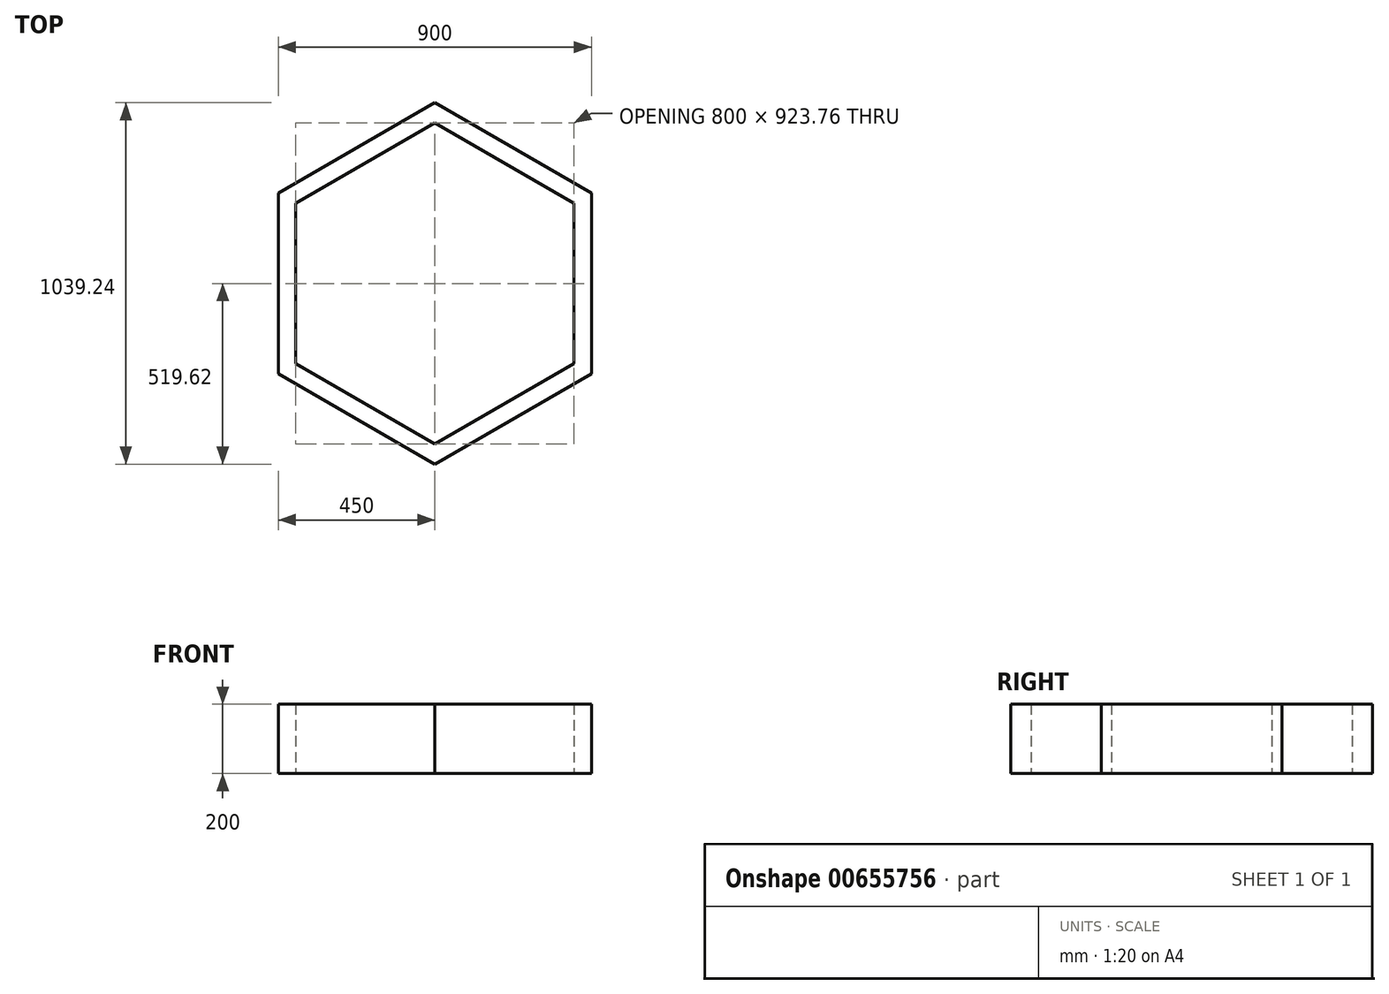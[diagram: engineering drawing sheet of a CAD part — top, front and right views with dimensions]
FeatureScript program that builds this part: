
annotation { "Feature Type Name" : "Feature", "Feature Type Description" : "" }
export const myFeature = defineFeature(function(context is Context, id is Id, definition is map)
    precondition{}
    {
        {
            var Q0;
            Q0=qCreatedBy(makeId("Top.planeOp"),FACE);
            var sketch = newSketch(context, id + "F0", { "sketchPlane" : qUnion([Q0])});
            skCircle(sketch, "E0.cCircle", {"center": v(0, 0) * mm, "radius": 450 * mm, "construction": true});
            skLineSegment(sketch, "E0.0", {"start": v(450, 259.8) * mm, "end": v(450, -259.8) * mm});
            skLineSegment(sketch, "E0.1", {"start": v(450, -259.8) * mm, "end": v(0, -519.62) * mm});
            skLineSegment(sketch, "E0.2", {"start": v(0, -519.62) * mm, "end": v(-450, -259.8) * mm});
            skLineSegment(sketch, "E0.3", {"start": v(-450, -259.8) * mm, "end": v(-450, 259.8) * mm});
            skLineSegment(sketch, "E0.4", {"start": v(-450, 259.8) * mm, "end": v(0, 519.62) * mm});
            skLineSegment(sketch, "E0.5", {"start": v(0, 519.62) * mm, "end": v(450, 259.8) * mm});
            skPoint(sketch, "E0.0.midPoint", {"position": v(450, 0) * mm});
            skCircle(sketch, "E1.cCircle", {"center": v(0, 0) * mm, "radius": 400 * mm, "construction": true});
            skLineSegment(sketch, "E1.0", {"start": v(400, 230.94) * mm, "end": v(400, -230.94) * mm});
            skLineSegment(sketch, "E1.1", {"start": v(400, -230.94) * mm, "end": v(0, -461.88) * mm});
            skLineSegment(sketch, "E1.2", {"start": v(0, -461.88) * mm, "end": v(-400, -230.94) * mm});
            skLineSegment(sketch, "E1.3", {"start": v(-400, -230.94) * mm, "end": v(-400, 230.94) * mm});
            skLineSegment(sketch, "E1.4", {"start": v(-400, 230.94) * mm, "end": v(0, 461.88) * mm});
            skLineSegment(sketch, "E1.5", {"start": v(0, 461.88) * mm, "end": v(400, 230.94) * mm});
            skPoint(sketch, "E1.0.midPoint", {"position": v(400, 0) * mm});
            skSolve(sketch);
        }
        {
            var Q0;
            Q0=makeQuery(id+"F0.imprint","IMPRINT",FACE,{"disambiguationData":[TD([[makeQuery(id+"F0.imprint","IMPRINT",EDGE,{"derivedFrom":sQuery(id+"F0.wireOp",EDGE,"E0.0")}),-1.0]])]});
            extrude(context, id + "F1", {"entities" : qUnion([Q0]), "depth" : 200 * mm, "offsetDistance" : 25 * mm});
        }
    });
